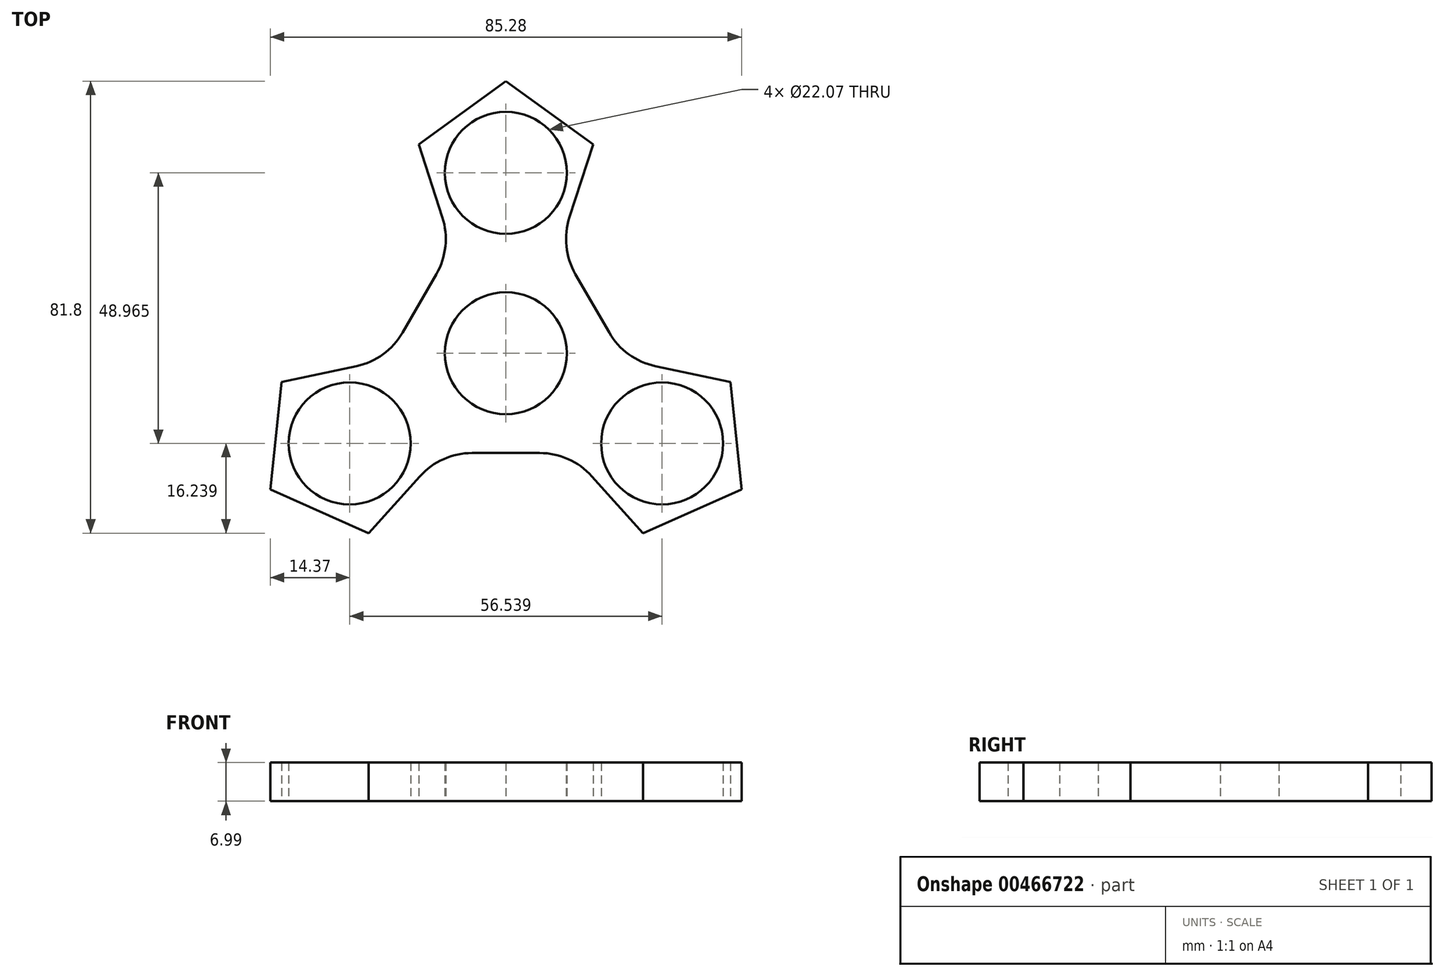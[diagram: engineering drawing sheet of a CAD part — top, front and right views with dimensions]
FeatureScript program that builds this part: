
annotation { "Feature Type Name" : "Feature", "Feature Type Description" : "" }
export const myFeature = defineFeature(function(context is Context, id is Id, definition is map)
    precondition{}
    {
        {
            var Q0;
            Q0=qCreatedBy(makeId("Top.planeOp"),FACE);
            var sketch = newSketch(context, id + "F0", { "sketchPlane" : qUnion([Q0])});
            skCircle(sketch, "E0", {"center": v(0, 0) * mm, "radius": 11.04 * mm});
            skCircle(sketch, "E1", {"center": v(0, 32.64) * mm, "radius": 11.04 * mm});
            skCircle(sketch, "E2.1.0", {"center": v(-28.27, -16.32) * mm, "radius": 11.04 * mm});
            skCircle(sketch, "E2.2.0", {"center": v(28.27, -16.32) * mm, "radius": 11.04 * mm});
            skCircle(sketch, "E3", {"center": v(0, 32.64) * mm, "radius": 13.43 * mm});
            skCircle(sketch, "E4", {"center": v(-28.27, -16.32) * mm, "radius": 13.43 * mm});
            skCircle(sketch, "E5", {"center": v(28.27, -16.32) * mm, "radius": 13.43 * mm});
            skCircle(sketch, "E6.cCircle", {"center": v(0, 32.64) * mm, "radius": 13.43 * mm, "construction": true});
            skLineSegment(sketch, "E6.1", {"start": v(-11.5, 24.6) * mm, "end": v(-15.79, 37.77) * mm});
            skLineSegment(sketch, "E6.2", {"start": v(-15.79, 37.77) * mm, "end": v(0, 49.24) * mm});
            skLineSegment(sketch, "E6.3", {"start": v(0, 49.24) * mm, "end": v(15.79, 37.77) * mm});
            skLineSegment(sketch, "E6.4", {"start": v(15.79, 37.77) * mm, "end": v(11.5, 24.6) * mm});
            skPoint(sketch, "E6.0.midPoint", {"position": v(0, 19.22) * mm});
            skLineSegment(sketch, "E7.1.0", {"start": v(-24.82, -32.56) * mm, "end": v(-42.64, -24.62) * mm});
            skLineSegment(sketch, "E7.1.1", {"start": v(-42.64, -24.62) * mm, "end": v(-40.6, -5.22) * mm});
            skLineSegment(sketch, "E7.2.0", {"start": v(40.6, -5.22) * mm, "end": v(42.64, -24.62) * mm});
            skLineSegment(sketch, "E7.2.1", {"start": v(42.64, -24.62) * mm, "end": v(24.82, -32.56) * mm});
            skPoint(sketch, "E8.visualSharp", {"position": v(-9.76, 19.22) * mm});
            skArc(sketch, "E8.filletArc", {"start": v(-12.58, 14.32) * mm, "mid": v(-10.95, 19.34) * mm, "end": v(-11.5, 24.6) * mm});
            skArc(sketch, "E9.1.0", {"start": v(-6.1, -18.06) * mm, "mid": v(-11.27, -19.15) * mm, "end": v(-15.55, -22.26) * mm});
            skArc(sketch, "E9.2.0", {"start": v(18.7, 3.74) * mm, "mid": v(22.23, -0.19) * mm, "end": v(27.05, -2.33) * mm});
            skPoint(sketch, "E10.visualSharp", {"position": v(9.76, 19.22) * mm});
            skArc(sketch, "E10.filletArc", {"start": v(11.5, 24.6) * mm, "mid": v(10.95, 19.34) * mm, "end": v(12.58, 14.32) * mm});
            skArc(sketch, "E11.1.0", {"start": v(-27.05, -2.33) * mm, "mid": v(-22.23, -0.19) * mm, "end": v(-18.7, 3.74) * mm});
            skArc(sketch, "E11.2.0", {"start": v(15.55, -22.26) * mm, "mid": v(11.27, -19.15) * mm, "end": v(6.1, -18.06) * mm});
            skLineSegment(sketch, "E12", {"start": v(12.58, 14.32) * mm, "end": v(18.7, 3.74) * mm});
            skLineSegment(sketch, "E13", {"start": v(27.05, -2.33) * mm, "end": v(40.6, -5.22) * mm});
            skLineSegment(sketch, "E14", {"start": v(-27.05, -2.33) * mm, "end": v(-40.6, -5.22) * mm});
            skLineSegment(sketch, "E15", {"start": v(-18.7, 3.74) * mm, "end": v(-12.58, 14.32) * mm});
            skLineSegment(sketch, "E16", {"start": v(-15.55, -22.26) * mm, "end": v(-24.82, -32.56) * mm});
            skLineSegment(sketch, "E17", {"start": v(-6.1, -18.06) * mm, "end": v(6.1, -18.06) * mm});
            skLineSegment(sketch, "E18", {"start": v(15.55, -22.26) * mm, "end": v(24.82, -32.56) * mm});
            skSolve(sketch);
        }
        {
            var Q0;
            Q0 = qSketchRegion(id + "F0", true);
            extrude(context, id + "F1", {"entities" : qUnion([Q0]), "depth" : 7 * mm});
        }
    });
